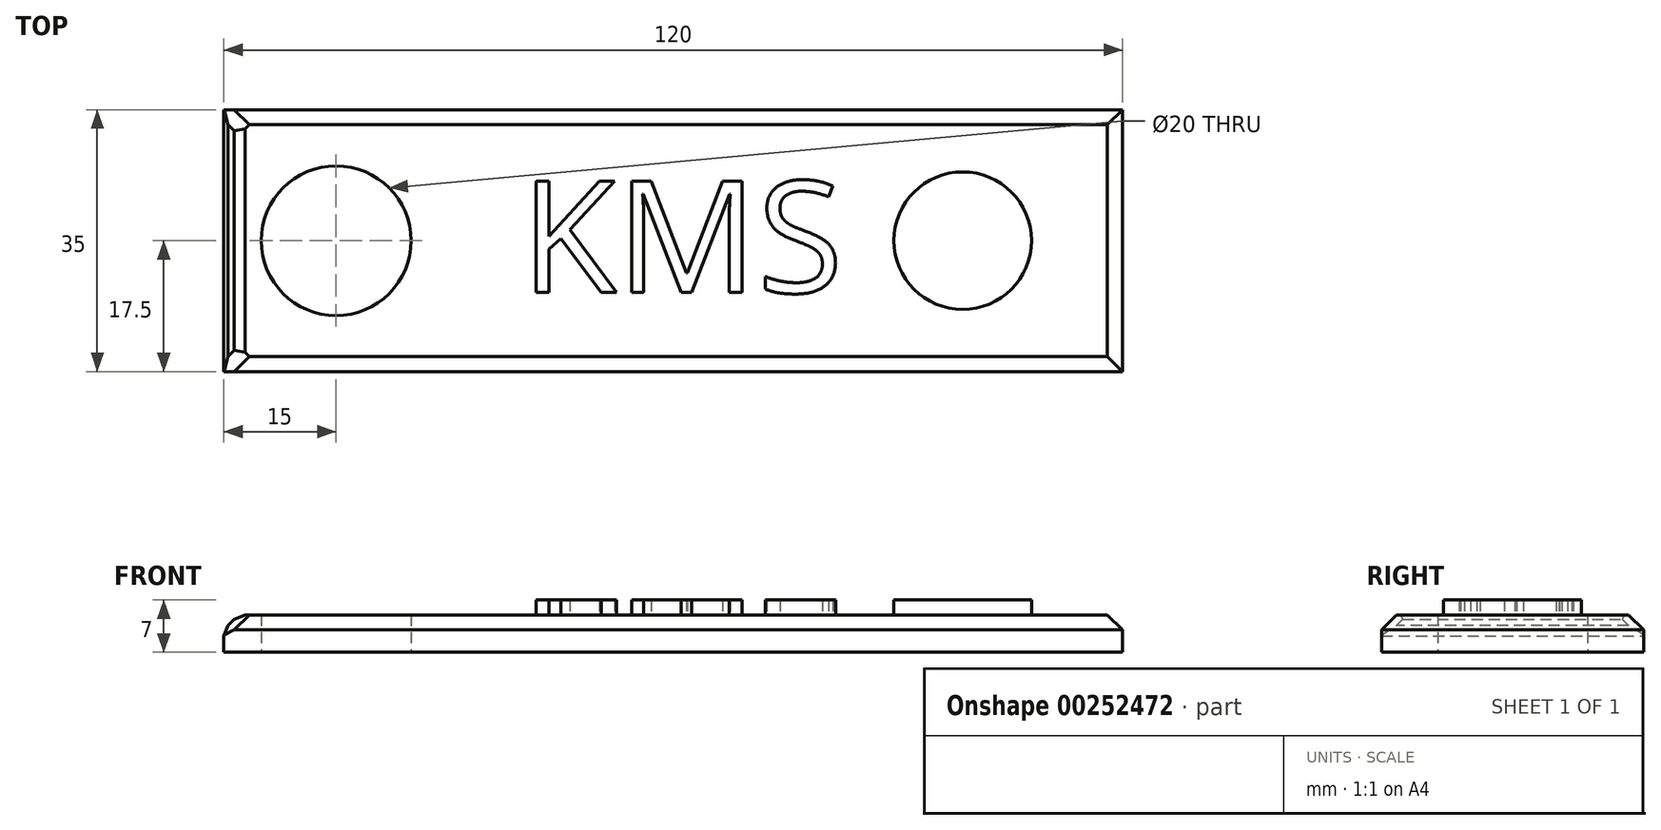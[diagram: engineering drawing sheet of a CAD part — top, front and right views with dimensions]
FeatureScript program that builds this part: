
annotation { "Feature Type Name" : "Feature", "Feature Type Description" : "" }
export const myFeature = defineFeature(function(context is Context, id is Id, definition is map)
    precondition{}
    {
        {
            var Q0;
            Q0=qCreatedBy(makeId("Top.planeOp"),FACE);
            var sketch = newSketch(context, id + "F0", { "sketchPlane" : qUnion([Q0])});
            skPoint(sketch, "E0.middle", {"position": v(0, 0) * mm});
            skLineSegment(sketch, "E1.bottom", {"start": v(-60, 17.5) * mm, "end": v(60, 17.5) * mm});
            skLineSegment(sketch, "E1.top", {"start": v(-60, -17.5) * mm, "end": v(60, -17.5) * mm});
            skLineSegment(sketch, "E1.left", {"start": v(-60, 17.5) * mm, "end": v(-60, -17.5) * mm});
            skLineSegment(sketch, "E1.right", {"start": v(60, 17.5) * mm, "end": v(60, -17.5) * mm});
            skCircle(sketch, "E2", {"center": v(-45, 0) * mm, "radius": 10 * mm});
            skPoint(sketch, "E2.centerSnap0", {"position": v(-60, 0) * mm});
            skSolve(sketch);
        }
        {
            var Q0;
            Q0=makeQuery(id+"F0.imprint","IMPRINT",FACE,{"disambiguationData":[TD([[makeQuery(id+"F0.imprint","IMPRINT",EDGE,{"derivedFrom":sQuery(id+"F0.wireOp",EDGE,"E1.bottom")}),-1.0]])]});
            extrude(context, id + "F1", {"entities" : qUnion([Q0]), "depth" : 5 * mm});
        }
        {
            var Q0;
            Q0=makeQuery(id+"F1.opExtrude","CAP_EDGE",EDGE,{"disambiguationData":[OSD([sQuery(id+"F0.wireOp",EDGE,"E1.right")])],"isStart":false});
            var Q1;
            Q1=makeQuery(id+"F1.opExtrude","CAP_EDGE",EDGE,{"disambiguationData":[OSD([sQuery(id+"F0.wireOp",EDGE,"E1.top")])],"isStart":false});
            var Q2;
            Q2=makeQuery(id+"F1.opExtrude","CAP_EDGE",EDGE,{"disambiguationData":[OSD([sQuery(id+"F0.wireOp",EDGE,"E1.left")])],"isStart":false});
            var Q3;
            Q3=makeQuery(id+"F1.opExtrude","CAP_EDGE",EDGE,{"disambiguationData":[OSD([sQuery(id+"F0.wireOp",EDGE,"E1.bottom")])],"isStart":false});
            chamfer(context, id + "F2", {"entities" : qUnion([Q0, Q1, Q2, Q3]), "width" : 2 * mm, "tangentPropagation" : true});
        }
        {
            var Q0;
            Q0=makeQuery(id+"F1.opExtrude","CAP_FACE",FACE,{"disambiguationData":[OSD([sQuery(id+"F0.wireOp",EDGE,"E1.bottom"),sQuery(id+"F0.wireOp",EDGE,"E1.top"),sQuery(id+"F0.wireOp",EDGE,"E1.left"),sQuery(id+"F0.wireOp",EDGE,"E1.right"),sQuery(id+"F0.wireOp",EDGE,"E2")])],"isStart":false});
            var sketch = newSketch(context, id + "F3", { "sketchPlane" : qUnion([Q0])});
            skSolve(sketch);
        }
        {
            var Q0;
            {var subQ0=sQuery(id+"F0.wireOp",EDGE,"E2");Q0=makeQuery(id+"F3.imprint","IMPRINT",FACE,{"disambiguationData":[TD([[makeQuery(id+"F3.imprint","IMPRINT",EDGE,{"derivedFrom":makeQuery(id+"F1.opExtrude","CAP_EDGE",EDGE,{"disambiguationData":[OSD([subQ0])],"isStart":false})}),-1.0]])]});}
            var sketch = newSketch(context, id + "F4", { "sketchPlane" : qUnion([Q0])});
            skText(sketch, "E3", { "text": "KMS", "fontName": "OpenSans-Regular.ttf"});
            const initialGuessF4  = {"E3": [-0.02035, -0.00693, 1, 0, 0.015]};
            skSetInitialGuess(sketch, initialGuessF4);
            skSolve(sketch);
        }
        {
            var Q0;
            {var subQ0=sQuery(id+"F0.wireOp",EDGE,"E2");Q0=makeQuery(id+"F3.imprint","IMPRINT",FACE,{"disambiguationData":[TD([[makeQuery(id+"F3.imprint","IMPRINT",EDGE,{"derivedFrom":makeQuery(id+"F1.opExtrude","CAP_EDGE",EDGE,{"disambiguationData":[OSD([subQ0])],"isStart":false})}),-1.0]])]});}
            var sketch = newSketch(context, id + "F5", { "sketchPlane" : qUnion([Q0])});
            skCircle(sketch, "E4", {"center": v(38.67, 0) * mm, "radius": 9.19 * mm});
            skSolve(sketch);
        }
        {
            var Q0;
            Q0 = qSketchRegion(id + "F4", true);
            extrude(context, id + "F6", {"entities" : qUnion([Q0]), "operationType" : NewBodyOperationType.ADD, "depth" : 2 * mm});
        }
        {
            var Q0;
            Q0=makeQuery(id+"F5.imprint","IMPRINT",FACE,{"disambiguationData":[TD([[makeQuery(id+"F5.imprint","IMPRINT",EDGE,{"derivedFrom":sQuery(id+"F5.wireOp",EDGE,"E4")}),1.0]])]});
            extrude(context, id + "F7", {"entities" : qUnion([Q0]), "operationType" : NewBodyOperationType.ADD, "depth" : 2 * mm});
        }
        {
            var Q0;
            Q0=makeQuery(id+"F2.opChamfer","BLEND_FACE",FACE,{"disambiguationData":[OSD([sQuery(id+"F0.wireOp",EDGE,"E1.left")])]});
            var Q1;
            {var subQ0=sQuery(id+"F0.wireOp",EDGE,"E1.left");Q1=makeQuery(id+"F2.opChamfer","BLEND_EDGE",EDGE,{"disambiguationData":[OD(1.0)],"blendedFrom":[makeQuery(id+"F1.opExtrude","CAP_EDGE",EDGE,{"disambiguationData":[OSD([subQ0])],"isStart":false}),makeQuery(id+"F1.opExtrude","CAP_FACE",FACE,{"disambiguationData":[OSD([sQuery(id+"F0.wireOp",EDGE,"E1.bottom"),sQuery(id+"F0.wireOp",EDGE,"E1.top"),subQ0,sQuery(id+"F0.wireOp",EDGE,"E1.right"),sQuery(id+"F0.wireOp",EDGE,"E2")])],"isStart":false})],"blendedInto":[makeQuery(id+"F1.opExtrude","CAP_FACE",FACE,{"disambiguationData":[OSD([sQuery(id+"F0.wireOp",EDGE,"E1.bottom"),sQuery(id+"F0.wireOp",EDGE,"E1.top"),subQ0,sQuery(id+"F0.wireOp",EDGE,"E1.right"),sQuery(id+"F0.wireOp",EDGE,"E2")])],"isStart":false})]});}
            chamfer(context, id + "F8", {"entities" : qUnion([Q0, Q1]), "width" : 2 * mm, "tangentPropagation" : true});
        }
    });
